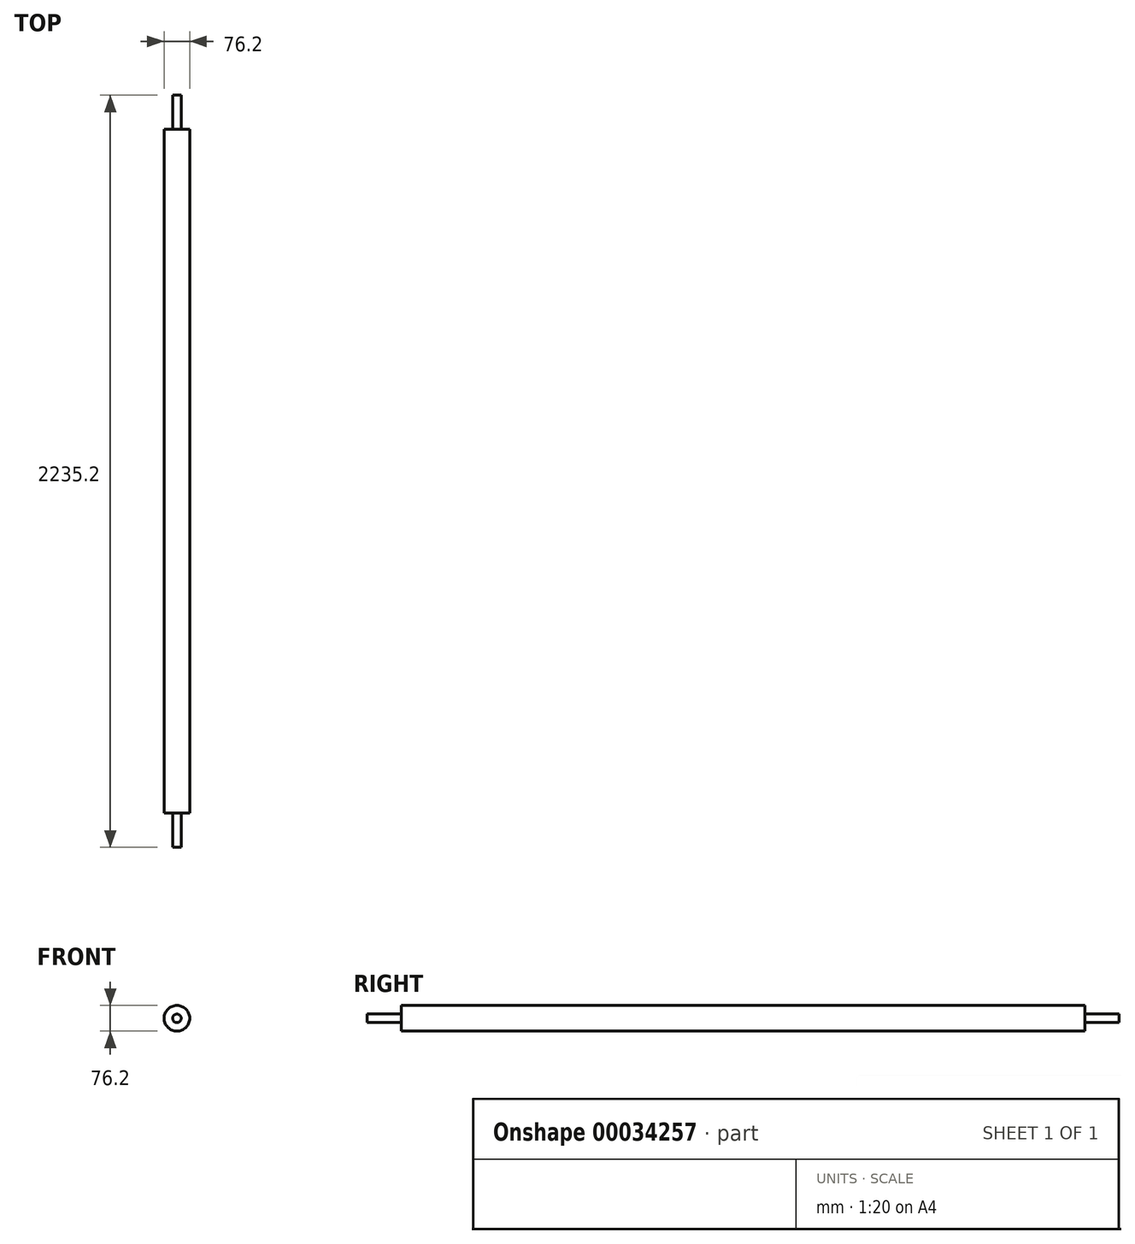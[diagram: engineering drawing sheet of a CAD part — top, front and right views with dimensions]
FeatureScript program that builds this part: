
annotation { "Feature Type Name" : "Feature", "Feature Type Description" : "" }
export const myFeature = defineFeature(function(context is Context, id is Id, definition is map)
    precondition{}
    {
        {
            var Q0;
            Q0=qCreatedBy(makeId("Front.planeOp"),FACE);
            var sketch = newSketch(context, id + "F0", { "sketchPlane" : qUnion([Q0])});
            skCircle(sketch, "E0", {"center": v(0, 0) * mm, "radius": 38.1 * mm});
            skSolve(sketch);
        }
        {
            var Q0;
            Q0=makeQuery(id+"F0.imprint","IMPRINT",FACE,{"disambiguationData":[TD([[makeQuery(id+"F0.imprint","IMPRINT",EDGE,{"derivedFrom":sQuery(id+"F0.wireOp",EDGE,"E0")}),1.0]])]});
            extrude(context, id + "F1", {"entities" : qUnion([Q0]), "depth" : 2235.2 * mm});
        }
        {
            var Q0;
            Q0=makeQuery(id+"F1.opExtrude","CAP_FACE",FACE,{"disambiguationData":[OSD([sQuery(id+"F0.wireOp",EDGE,"E0")])],"isStart":false});
            var sketch = newSketch(context, id + "F2", { "sketchPlane" : qUnion([Q0])});
            skCircle(sketch, "E1", {"center": v(0, 0) * mm, "radius": 12.7 * mm});
            skSolve(sketch);
        }
        {
            var Q0;
            Q0=makeQuery(id+"F2.imprint","IMPRINT",FACE,{"disambiguationData":[TD([[makeQuery(id+"F2.imprint","IMPRINT",EDGE,{"derivedFrom":sQuery(id+"F2.wireOp",EDGE,"E1")}),-1.0]])]});
            extrude(context, id + "F3", {"entities" : qUnion([Q0]), "operationType" : NewBodyOperationType.REMOVE, "oppositeDirection" : true, "depth" : 101.6 * mm});
        }
        {
            var Q0;
            Q0=makeQuery(id+"F1.opExtrude","CAP_FACE",FACE,{"disambiguationData":[OSD([sQuery(id+"F0.wireOp",EDGE,"E0")])],"isStart":true});
            var sketch = newSketch(context, id + "F4", { "sketchPlane" : qUnion([Q0])});
            skCircle(sketch, "E2", {"center": v(0, 0) * mm, "radius": 12.7 * mm});
            skSolve(sketch);
        }
        {
            var Q0;
            Q0=makeQuery(id+"F4.imprint","IMPRINT",FACE,{"disambiguationData":[TD([[makeQuery(id+"F4.imprint","IMPRINT",EDGE,{"derivedFrom":sQuery(id+"F4.wireOp",EDGE,"E2")}),-1.0]])]});
            extrude(context, id + "F5", {"entities" : qUnion([Q0]), "operationType" : NewBodyOperationType.REMOVE, "oppositeDirection" : true, "depth" : 101.6 * mm});
        }
    });
